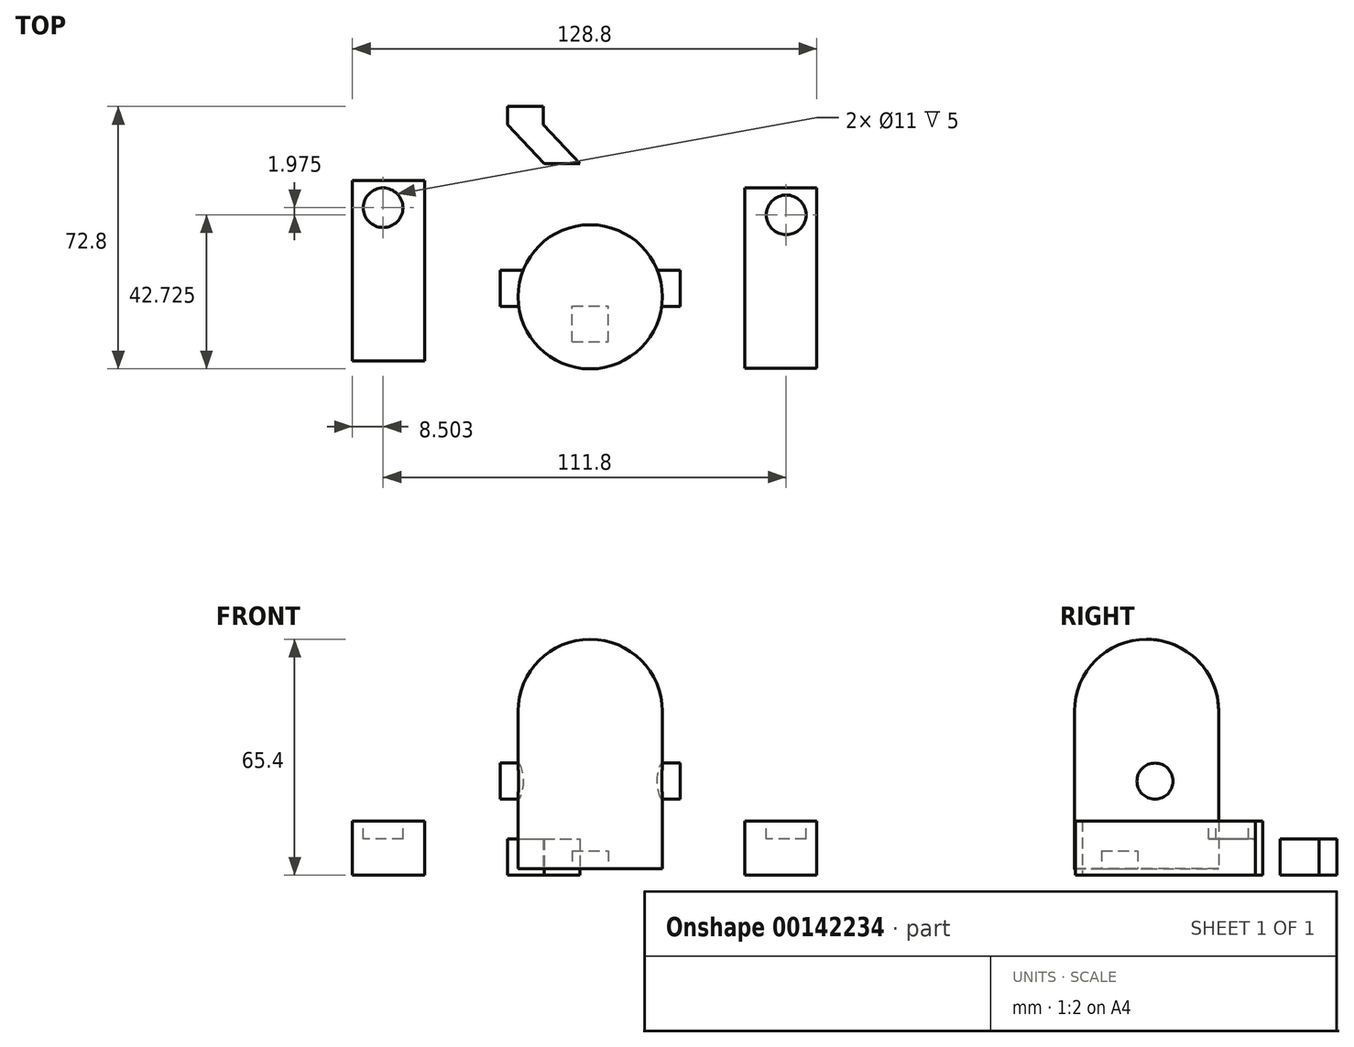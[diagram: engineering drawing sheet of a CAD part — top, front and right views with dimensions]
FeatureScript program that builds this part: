
annotation { "Feature Type Name" : "Feature", "Feature Type Description" : "" }
export const myFeature = defineFeature(function(context is Context, id is Id, definition is map)
    precondition{}
    {
        {
            var Q0;
            Q0=qCreatedBy(makeId("Right.planeOp"),FACE);
            var sketch = newSketch(context, id + "F0", { "sketchPlane" : qUnion([Q0])});
            skArc(sketch, "E0", {"start": v(16.89, 45.4) * mm, "mid": v(11.03, 59.54) * mm, "end": v(-3.1, 65.4) * mm});
            skLineSegment(sketch, "E1", {"start": v(-3.1, 1.75) * mm, "end": v(16.89, 1.75) * mm});
            skLineSegment(sketch, "E2", {"start": v(16.89, 1.75) * mm, "end": v(16.89, 45.4) * mm});
            skLineSegment(sketch, "E3", {"start": v(-3.1, 45.4) * mm, "end": v(-3.1, 1.75) * mm});
            skPoint(sketch, "E3.endSnap0", {"position": v(-3.1, 1.75) * mm});
            skLineSegment(sketch, "E4", {"start": v(-3.1, 45.4) * mm, "end": v(-3.1, 65.4) * mm});
            skSolve(sketch);
        }
        {
            var Q0;
            Q0=makeQuery(id+"F0.imprint","IMPRINT",FACE,{"disambiguationData":[TD([[makeQuery(id+"F0.imprint","IMPRINT",EDGE,{"derivedFrom":sQuery(id+"F0.wireOp",EDGE,"E0")}),1.0]])]});
            var Q1;
            Q1=sQuery(id+"F0.wireOp",EDGE,"E4");
            revolve(context, id + "F1", {"entities" : qUnion([Q0]), "axis" : qUnion([Q1]), "revolveType" : RevolveType.FULL});
        }
        {
            var Q0;
            Q0=qCreatedBy(makeId("Right.planeOp"),FACE);
            var sketch = newSketch(context, id + "F2", { "sketchPlane" : qUnion([Q0])});
            skCircle(sketch, "E5", {"center": v(-0.77, 26.06) * mm, "radius": 5 * mm});
            skSolve(sketch);
        }
        {
            var Q0;
            Q0 = qSketchRegion(id + "F2", true);
            var Q1;
            Q1=sQuery(id+"F2.wireOp",EDGE,"E5");
            extrude(context, id + "F3", {"entities" : qUnion([Q0]), "operationType" : NewBodyOperationType.ADD, "surfaceEntities" : qUnion([Q1]), "endBound" : BoundingType.SYMMETRIC, "oppositeDirection" : true, "depth" : 50 * mm});
        }
        {
            var Q0;
            Q0=qCreatedBy(makeId("Top.planeOp"),FACE);
            var sketch = newSketch(context, id + "F4", { "sketchPlane" : qUnion([Q0])});
            skLineSegment(sketch, "E6.bottom", {"start": v(42.86, 27.13) * mm, "end": v(62.86, 27.13) * mm});
            skLineSegment(sketch, "E6.top", {"start": v(42.86, -22.87) * mm, "end": v(62.86, -22.87) * mm});
            skLineSegment(sketch, "E6.left", {"start": v(42.86, 27.13) * mm, "end": v(42.86, -22.87) * mm});
            skLineSegment(sketch, "E6.right", {"start": v(62.86, 27.13) * mm, "end": v(62.86, -22.87) * mm});
            skLineSegment(sketch, "E7.bottom", {"start": v(-65.94, 29.1) * mm, "end": v(-45.94, 29.1) * mm});
            skLineSegment(sketch, "E7.top", {"start": v(-65.94, -20.9) * mm, "end": v(-45.94, -20.9) * mm});
            skLineSegment(sketch, "E7.left", {"start": v(-65.94, 29.1) * mm, "end": v(-65.94, -20.9) * mm});
            skLineSegment(sketch, "E7.right", {"start": v(-45.94, 29.1) * mm, "end": v(-45.94, -20.9) * mm});
            skSolve(sketch);
        }
        {
            var Q0;
            Q0=makeQuery(id+"F4.imprint","IMPRINT",FACE,{"disambiguationData":[TD([[makeQuery(id+"F4.imprint","IMPRINT",EDGE,{"derivedFrom":sQuery(id+"F4.wireOp",EDGE,"E7.bottom")}),-1.0]])]});
            var Q1;
            Q1=makeQuery(id+"F4.imprint","IMPRINT",FACE,{"disambiguationData":[TD([[makeQuery(id+"F4.imprint","IMPRINT",EDGE,{"derivedFrom":sQuery(id+"F4.wireOp",EDGE,"E6.bottom")}),-1.0]])]});
            extrude(context, id + "F5", {"entities" : qUnion([Q0, Q1]), "depth" : 15 * mm});
        }
        {
            var Q0;
            Q0=makeQuery(id+"F5.opExtrude","CAP_FACE",FACE,{"disambiguationData":[OSD([sQuery(id+"F4.wireOp",EDGE,"E7.bottom"),sQuery(id+"F4.wireOp",EDGE,"E7.top"),sQuery(id+"F4.wireOp",EDGE,"E7.left"),sQuery(id+"F4.wireOp",EDGE,"E7.right")])],"isStart":false});
            var sketch = newSketch(context, id + "F6", { "sketchPlane" : qUnion([Q0])});
            skCircle(sketch, "E8", {"center": v(-57.44, 21.6) * mm, "radius": 5.5 * mm});
            skSolve(sketch);
        }
        {
            var Q0;
            Q0=makeQuery(id+"F5.opExtrude","CAP_FACE",FACE,{"disambiguationData":[OSD([sQuery(id+"F4.wireOp",EDGE,"E6.bottom"),sQuery(id+"F4.wireOp",EDGE,"E6.top"),sQuery(id+"F4.wireOp",EDGE,"E6.left"),sQuery(id+"F4.wireOp",EDGE,"E6.right")])],"isStart":false});
            var sketch = newSketch(context, id + "F7", { "sketchPlane" : qUnion([Q0])});
            skCircle(sketch, "E9", {"center": v(54.36, 19.63) * mm, "radius": 5.5 * mm});
            skSolve(sketch);
        }
        {
            var Q0;
            Q0=makeQuery(id+"F6.imprint","IMPRINT",FACE,{"disambiguationData":[TD([[makeQuery(id+"F6.imprint","IMPRINT",EDGE,{"derivedFrom":sQuery(id+"F6.wireOp",EDGE,"E8")}),1.0]])]});
            extrude(context, id + "F8", {"entities" : qUnion([Q0]), "operationType" : NewBodyOperationType.REMOVE, "oppositeDirection" : true, "depth" : 5 * mm});
        }
        {
            var Q0;
            Q0=makeQuery(id+"F7.imprint","IMPRINT",FACE,{"disambiguationData":[TD([[makeQuery(id+"F7.imprint","IMPRINT",EDGE,{"derivedFrom":sQuery(id+"F7.wireOp",EDGE,"E9")}),1.0]])]});
            extrude(context, id + "F9", {"entities" : qUnion([Q0]), "operationType" : NewBodyOperationType.REMOVE, "oppositeDirection" : true, "depth" : 5 * mm});
        }
        {
            var Q0;
            Q0=makeQuery(id+"F1.opRevolve","SWEPT_FACE",FACE,{"disambiguationData":[OSD([sQuery(id+"F0.wireOp",EDGE,"E1")])]});
            var sketch = newSketch(context, id + "F10", { "sketchPlane" : qUnion([Q0])});
            skLineSegment(sketch, "E10.bottom", {"start": v(-5, 15.6) * mm, "end": v(5, 15.6) * mm});
            skLineSegment(sketch, "E10.top", {"start": v(-5, 5.6) * mm, "end": v(5, 5.6) * mm});
            skLineSegment(sketch, "E10.left", {"start": v(-5, 15.6) * mm, "end": v(-5, 5.6) * mm});
            skLineSegment(sketch, "E10.right", {"start": v(5, 15.6) * mm, "end": v(5, 5.6) * mm});
            skSolve(sketch);
        }
        {
            var Q0;
            Q0=makeQuery(id+"F10.imprint","IMPRINT",FACE,{"disambiguationData":[TD([[makeQuery(id+"F10.imprint","IMPRINT",EDGE,{"derivedFrom":sQuery(id+"F10.wireOp",EDGE,"E10.bottom")}),-1.0]])]});
            extrude(context, id + "F11", {"entities" : qUnion([Q0]), "operationType" : NewBodyOperationType.REMOVE, "oppositeDirection" : true, "depth" : 5 * mm});
        }
        {
            var Q0;
            Q0=qCreatedBy(makeId("Top.planeOp"),FACE);
            var sketch = newSketch(context, id + "F12", { "sketchPlane" : qUnion([Q0])});
            skLineSegment(sketch, "E11", {"start": v(-22.97, 49.7) * mm, "end": v(-12.98, 49.7) * mm});
            skLineSegment(sketch, "E12", {"start": v(-22.97, 49.7) * mm, "end": v(-22.97, 44.7) * mm});
            skLineSegment(sketch, "E13", {"start": v(-22.97, 44.7) * mm, "end": v(-12.8, 33.88) * mm});
            skLineSegment(sketch, "E14", {"start": v(-12.8, 33.88) * mm, "end": v(-2.8, 33.88) * mm});
            skLineSegment(sketch, "E15", {"start": v(-12.98, 49.7) * mm, "end": v(-12.98, 44.7) * mm});
            skLineSegment(sketch, "E16", {"start": v(-12.98, 44.7) * mm, "end": v(-2.8, 33.88) * mm});
            skSolve(sketch);
        }
        {
            var Q0;
            Q0=makeQuery(id+"F12.imprint","IMPRINT",FACE,{"disambiguationData":[TD([[makeQuery(id+"F12.imprint","IMPRINT",EDGE,{"derivedFrom":sQuery(id+"F12.wireOp",EDGE,"E11")}),-1.0]])]});
            extrude(context, id + "F13", {"entities" : qUnion([Q0]), "depth" : 10 * mm});
        }
    });
